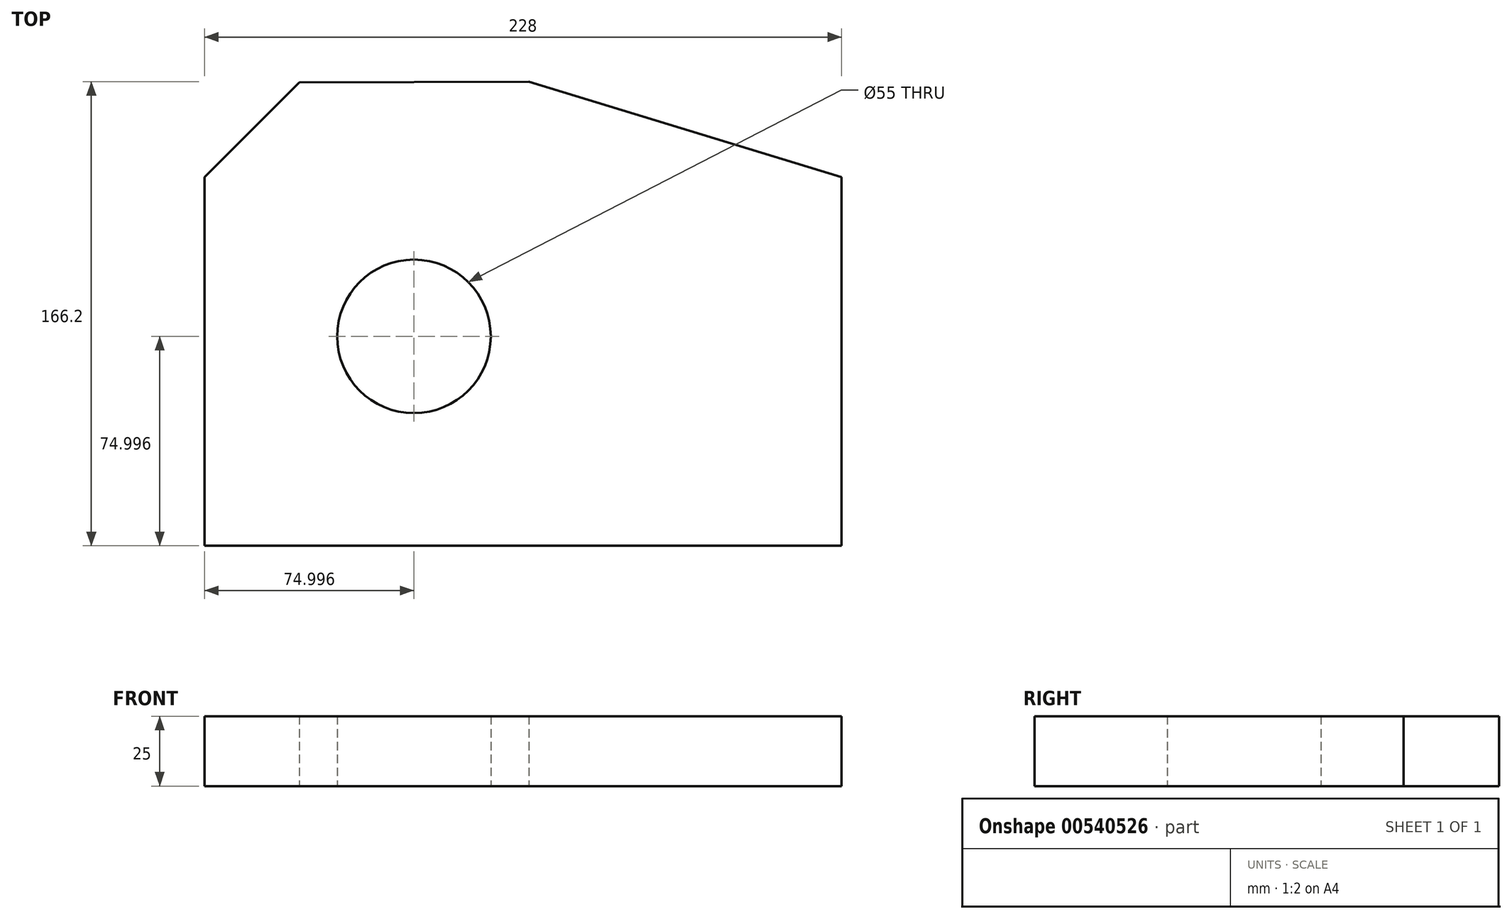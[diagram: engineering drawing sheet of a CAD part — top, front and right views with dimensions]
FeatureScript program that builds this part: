
annotation { "Feature Type Name" : "Feature", "Feature Type Description" : "" }
export const myFeature = defineFeature(function(context is Context, id is Id, definition is map)
    precondition{}
    {
        {
            var Q0;
            Q0=qCreatedBy(makeId("Top.planeOp"),FACE);
            var sketch = newSketch(context, id + "F0", { "sketchPlane" : qUnion([Q0])});
            skLineSegment(sketch, "E0", {"start": v(-97.36, -48.12) * mm, "end": v(130.64, -48.12) * mm});
            skLineSegment(sketch, "E1", {"start": v(130.64, -48.12) * mm, "end": v(130.64, 83.88) * mm});
            skLineSegment(sketch, "E2", {"start": v(130.64, 83.88) * mm, "end": v(18.75, 118.08) * mm});
            skLineSegment(sketch, "E3", {"start": v(-97.36, -48.12) * mm, "end": v(-97.36, 83.88) * mm});
            skCircle(sketch, "E4", {"center": v(-22.36, 26.88) * mm, "radius": 27.5 * mm});
            skLineSegment(sketch, "E5", {"start": v(-97.36, 83.88) * mm, "end": v(-63.42, 117.82) * mm});
            skLineSegment(sketch, "E6", {"start": v(-63.42, 117.82) * mm, "end": v(18.75, 118.08) * mm});
            skSolve(sketch);
        }
        {
            var Q0;
            Q0=makeQuery(id+"F0.imprint","IMPRINT",FACE,{"disambiguationData":[TD([[makeQuery(id+"F0.imprint","IMPRINT",EDGE,{"derivedFrom":sQuery(id+"F0.wireOp",EDGE,"E0")}),1.0]])]});
            extrude(context, id + "F1", {"entities" : qUnion([Q0]), "depth" : 25 * mm, "offsetDistance" : 25 * mm});
        }
    });
